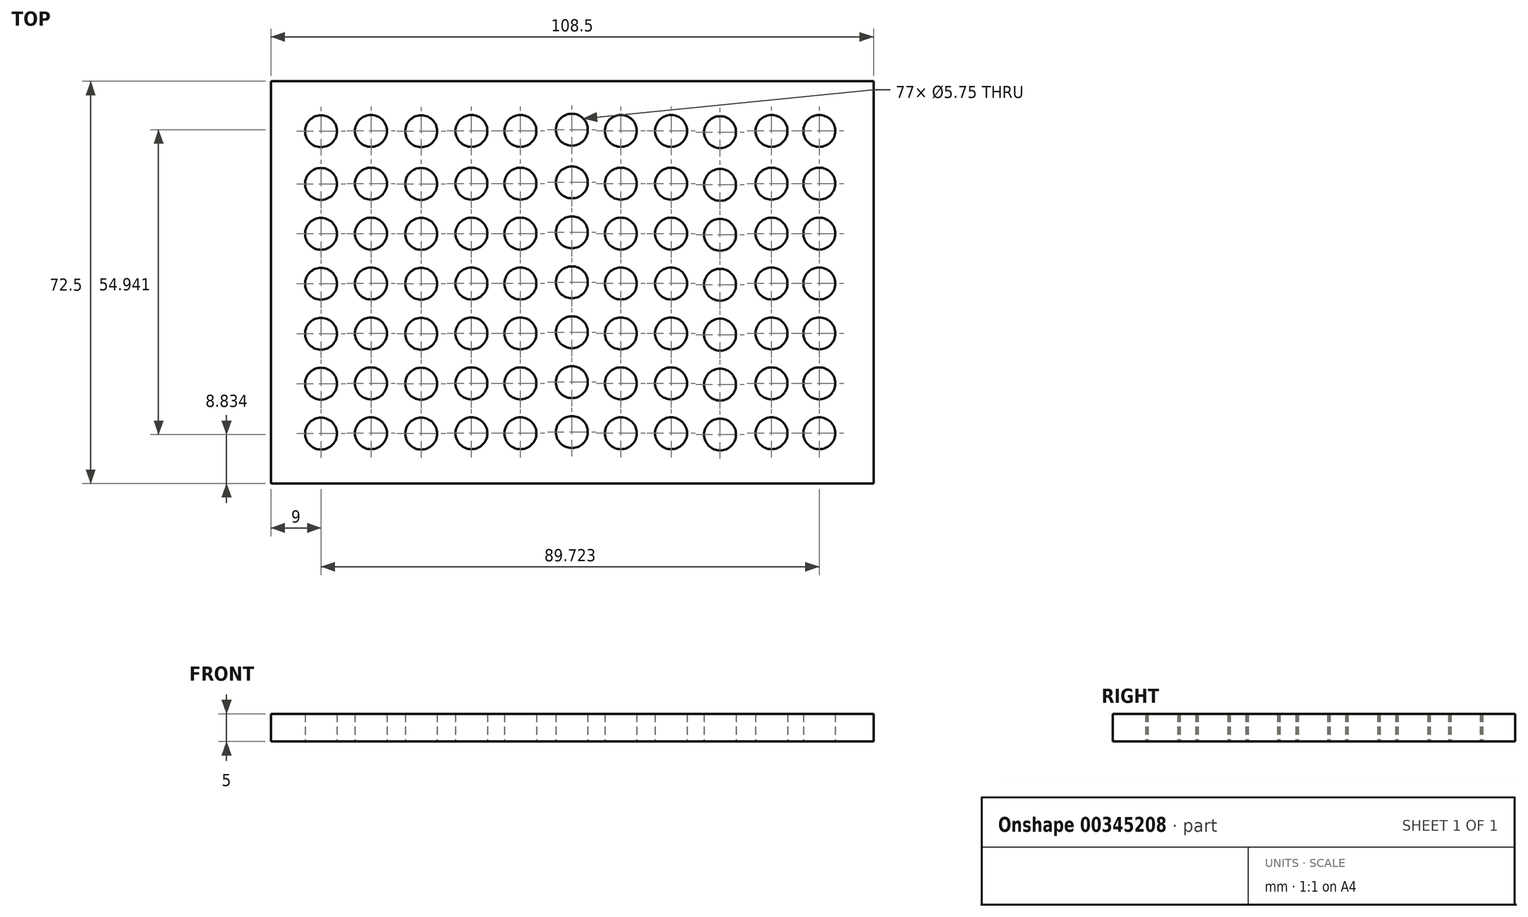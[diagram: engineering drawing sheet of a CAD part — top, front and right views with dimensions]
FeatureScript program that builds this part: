
annotation { "Feature Type Name" : "Feature", "Feature Type Description" : "" }
export const myFeature = defineFeature(function(context is Context, id is Id, definition is map)
    precondition{}
    {
        {
            var Q0;
            Q0=qCreatedBy(makeId("Top.planeOp"),FACE);
            var sketch = newSketch(context, id + "F0", { "sketchPlane" : qUnion([Q0])});
            skLineSegment(sketch, "E0", {"start": v(0, 0) * mm, "end": v(0, 72.5) * mm});
            skLineSegment(sketch, "E1", {"start": v(0, 0) * mm, "end": v(108.5, 0) * mm});
            skLineSegment(sketch, "E2", {"start": v(0, 72.5) * mm, "end": v(108.5, 72.5) * mm});
            skLineSegment(sketch, "E3", {"start": v(108.5, 72.5) * mm, "end": v(108.5, 0) * mm});
            skLineSegment(sketch, "E4", {"start": v(0, 0) * mm, "end": v(9, 0) * mm});
            skLineSegment(sketch, "E5", {"start": v(0, 72.5) * mm, "end": v(0, 63.5) * mm});
            skLineSegment(sketch, "E6", {"start": v(0, 0) * mm, "end": v(0, 9) * mm});
            skLineSegment(sketch, "E7", {"start": v(108.5, 9) * mm, "end": v(108.5, 18) * mm});
            skLineSegment(sketch, "E8", {"start": v(0, 18) * mm, "end": v(0, 27) * mm});
            skLineSegment(sketch, "E9", {"start": v(108.5, 27) * mm, "end": v(108.5, 36) * mm});
            skLineSegment(sketch, "E10", {"start": v(0, 36) * mm, "end": v(0, 45) * mm});
            skLineSegment(sketch, "E11", {"start": v(108.5, 45) * mm, "end": v(108.5, 54) * mm});
            skLineSegment(sketch, "E12", {"start": v(9, 72.5) * mm, "end": v(18, 72.5) * mm});
            skLineSegment(sketch, "E13", {"start": v(18, 72.5) * mm, "end": v(27, 72.5) * mm});
            skLineSegment(sketch, "E14", {"start": v(27, 72.5) * mm, "end": v(36, 72.5) * mm});
            skLineSegment(sketch, "E15", {"start": v(36, 72.5) * mm, "end": v(54.25, 72.5) * mm});
            skLineSegment(sketch, "E16", {"start": v(36, 72.5) * mm, "end": v(45, 72.5) * mm});
            skLineSegment(sketch, "E17", {"start": v(45, 72.5) * mm, "end": v(54, 72.5) * mm});
            skLineSegment(sketch, "E18", {"start": v(54, 72.5) * mm, "end": v(63, 72.5) * mm});
            skLineSegment(sketch, "E19", {"start": v(63, 72.5) * mm, "end": v(72, 72.5) * mm});
            skLineSegment(sketch, "E20", {"start": v(72, 72.5) * mm, "end": v(81, 72.5) * mm});
            skLineSegment(sketch, "E21", {"start": v(81, 72.5) * mm, "end": v(90, 72.5) * mm});
            skLineSegment(sketch, "E22", {"start": v(90, 72.5) * mm, "end": v(99, 72.5) * mm});
            skLineSegment(sketch, "E23", {"start": v(99, 72.5) * mm, "end": v(108.5, 72.5) * mm});
            skCircle(sketch, "E24", {"center": v(9, 63.5) * mm, "radius": 2.88 * mm});
            skCircle(sketch, "E25", {"center": v(9, 54) * mm, "radius": 2.88 * mm});
            skCircle(sketch, "E26", {"center": v(9, 45) * mm, "radius": 2.88 * mm});
            skCircle(sketch, "E27", {"center": v(9, 36) * mm, "radius": 2.88 * mm});
            skPoint(sketch, "E27.centerSnap0", {"position": v(9, 36.25) * mm});
            skCircle(sketch, "E28", {"center": v(9, 27) * mm, "radius": 2.88 * mm});
            skCircle(sketch, "E29", {"center": v(9, 18) * mm, "radius": 2.88 * mm});
            skCircle(sketch, "E30", {"center": v(9, 9) * mm, "radius": 2.88 * mm});
            skCircle(sketch, "E31", {"center": v(18, 63.55) * mm, "radius": 2.88 * mm});
            skCircle(sketch, "E32", {"center": v(18, 54.05) * mm, "radius": 2.88 * mm});
            skCircle(sketch, "E33", {"center": v(18, 45.05) * mm, "radius": 2.88 * mm});
            skCircle(sketch, "E34", {"center": v(18, 36.05) * mm, "radius": 2.88 * mm});
            skPoint(sketch, "E34.centerSnap0", {"position": v(18, 36.3) * mm});
            skCircle(sketch, "E35", {"center": v(18, 27.05) * mm, "radius": 2.88 * mm});
            skCircle(sketch, "E36", {"center": v(18, 18.05) * mm, "radius": 2.88 * mm});
            skCircle(sketch, "E37", {"center": v(18, 9.05) * mm, "radius": 2.88 * mm});
            skCircle(sketch, "E38", {"center": v(27.04, 63.5) * mm, "radius": 2.88 * mm});
            skCircle(sketch, "E39", {"center": v(27.04, 54) * mm, "radius": 2.88 * mm});
            skCircle(sketch, "E40", {"center": v(27.04, 45) * mm, "radius": 2.88 * mm});
            skCircle(sketch, "E41", {"center": v(27.04, 36) * mm, "radius": 2.88 * mm});
            skPoint(sketch, "E41.centerSnap0", {"position": v(27.04, 36.25) * mm});
            skCircle(sketch, "E42", {"center": v(27.04, 27) * mm, "radius": 2.88 * mm});
            skCircle(sketch, "E43", {"center": v(27.04, 18) * mm, "radius": 2.88 * mm});
            skCircle(sketch, "E44", {"center": v(27.04, 9) * mm, "radius": 2.88 * mm});
            skCircle(sketch, "E45", {"center": v(36.08, 63.55) * mm, "radius": 2.88 * mm});
            skCircle(sketch, "E46", {"center": v(36.08, 54.05) * mm, "radius": 2.88 * mm});
            skCircle(sketch, "E47", {"center": v(36.08, 45.05) * mm, "radius": 2.88 * mm});
            skCircle(sketch, "E48", {"center": v(36.08, 36.05) * mm, "radius": 2.88 * mm});
            skPoint(sketch, "E48.centerSnap0", {"position": v(36.08, 36.3) * mm});
            skCircle(sketch, "E49", {"center": v(36.08, 27.05) * mm, "radius": 2.88 * mm});
            skCircle(sketch, "E50", {"center": v(36.08, 18.05) * mm, "radius": 2.88 * mm});
            skCircle(sketch, "E51", {"center": v(36.08, 9.05) * mm, "radius": 2.88 * mm});
            skCircle(sketch, "E52", {"center": v(44.9, 63.55) * mm, "radius": 2.88 * mm});
            skCircle(sketch, "E53", {"center": v(44.9, 54.05) * mm, "radius": 2.88 * mm});
            skCircle(sketch, "E54", {"center": v(44.9, 45.05) * mm, "radius": 2.88 * mm});
            skCircle(sketch, "E55", {"center": v(44.9, 36.05) * mm, "radius": 2.88 * mm});
            skPoint(sketch, "E55.centerSnap0", {"position": v(44.9, 36.3) * mm});
            skCircle(sketch, "E56", {"center": v(44.9, 27.05) * mm, "radius": 2.88 * mm});
            skCircle(sketch, "E57", {"center": v(44.9, 18.05) * mm, "radius": 2.88 * mm});
            skCircle(sketch, "E58", {"center": v(44.9, 9.05) * mm, "radius": 2.88 * mm});
            skCircle(sketch, "E59", {"center": v(54.17, 63.77) * mm, "radius": 2.88 * mm});
            skCircle(sketch, "E60", {"center": v(54.17, 54.27) * mm, "radius": 2.88 * mm});
            skCircle(sketch, "E61", {"center": v(54.17, 45.27) * mm, "radius": 2.88 * mm});
            skCircle(sketch, "E62", {"center": v(54.17, 36.27) * mm, "radius": 2.88 * mm});
            skPoint(sketch, "E62.centerSnap0", {"position": v(54.17, 36.52) * mm});
            skCircle(sketch, "E63", {"center": v(54.17, 27.27) * mm, "radius": 2.88 * mm});
            skCircle(sketch, "E64", {"center": v(54.17, 18.27) * mm, "radius": 2.88 * mm});
            skCircle(sketch, "E65", {"center": v(54.17, 9.27) * mm, "radius": 2.88 * mm});
            skCircle(sketch, "E66", {"center": v(63, 63.55) * mm, "radius": 2.88 * mm});
            skCircle(sketch, "E67", {"center": v(63, 54.05) * mm, "radius": 2.88 * mm});
            skCircle(sketch, "E68", {"center": v(63, 45.05) * mm, "radius": 2.88 * mm});
            skCircle(sketch, "E69", {"center": v(63, 36.05) * mm, "radius": 2.88 * mm});
            skPoint(sketch, "E69.centerSnap0", {"position": v(63, 36.3) * mm});
            skCircle(sketch, "E70", {"center": v(63, 27.05) * mm, "radius": 2.88 * mm});
            skCircle(sketch, "E71", {"center": v(63, 18.05) * mm, "radius": 2.88 * mm});
            skCircle(sketch, "E72", {"center": v(63, 9.05) * mm, "radius": 2.88 * mm});
            skCircle(sketch, "E73", {"center": v(72.03, 63.55) * mm, "radius": 2.88 * mm});
            skCircle(sketch, "E74", {"center": v(72.03, 54.05) * mm, "radius": 2.88 * mm});
            skCircle(sketch, "E75", {"center": v(72.03, 45.05) * mm, "radius": 2.88 * mm});
            skCircle(sketch, "E76", {"center": v(72.03, 36.05) * mm, "radius": 2.88 * mm});
            skPoint(sketch, "E76.centerSnap0", {"position": v(72.03, 36.3) * mm});
            skCircle(sketch, "E77", {"center": v(72.03, 27.05) * mm, "radius": 2.88 * mm});
            skCircle(sketch, "E78", {"center": v(72.03, 18.05) * mm, "radius": 2.88 * mm});
            skCircle(sketch, "E79", {"center": v(72.03, 9.05) * mm, "radius": 2.88 * mm});
            skCircle(sketch, "E80", {"center": v(80.86, 63.33) * mm, "radius": 2.88 * mm});
            skCircle(sketch, "E81", {"center": v(80.86, 53.83) * mm, "radius": 2.88 * mm});
            skCircle(sketch, "E82", {"center": v(80.86, 44.83) * mm, "radius": 2.88 * mm});
            skCircle(sketch, "E83", {"center": v(80.86, 35.83) * mm, "radius": 2.88 * mm});
            skPoint(sketch, "E83.centerSnap0", {"position": v(80.86, 36.08) * mm});
            skCircle(sketch, "E84", {"center": v(80.86, 26.83) * mm, "radius": 2.88 * mm});
            skCircle(sketch, "E85", {"center": v(80.86, 17.83) * mm, "radius": 2.88 * mm});
            skCircle(sketch, "E86", {"center": v(80.86, 8.83) * mm, "radius": 2.88 * mm});
            skCircle(sketch, "E87", {"center": v(90.12, 63.55) * mm, "radius": 2.88 * mm});
            skCircle(sketch, "E88", {"center": v(90.12, 54.05) * mm, "radius": 2.88 * mm});
            skCircle(sketch, "E89", {"center": v(90.12, 45.05) * mm, "radius": 2.88 * mm});
            skCircle(sketch, "E90", {"center": v(90.12, 36.05) * mm, "radius": 2.88 * mm});
            skPoint(sketch, "E90.centerSnap0", {"position": v(90.12, 36.3) * mm});
            skCircle(sketch, "E91", {"center": v(90.12, 27.05) * mm, "radius": 2.88 * mm});
            skCircle(sketch, "E92", {"center": v(90.12, 18.05) * mm, "radius": 2.88 * mm});
            skCircle(sketch, "E93", {"center": v(90.12, 9.05) * mm, "radius": 2.88 * mm});
            skCircle(sketch, "E94", {"center": v(98.72, 63.55) * mm, "radius": 2.88 * mm});
            skCircle(sketch, "E95", {"center": v(98.72, 54.05) * mm, "radius": 2.88 * mm});
            skCircle(sketch, "E96", {"center": v(98.72, 45.05) * mm, "radius": 2.88 * mm});
            skCircle(sketch, "E97", {"center": v(98.72, 36.05) * mm, "radius": 2.88 * mm});
            skPoint(sketch, "E97.centerSnap0", {"position": v(98.72, 36.3) * mm});
            skCircle(sketch, "E98", {"center": v(98.72, 27.05) * mm, "radius": 2.88 * mm});
            skCircle(sketch, "E99", {"center": v(98.72, 18.05) * mm, "radius": 2.88 * mm});
            skCircle(sketch, "E100", {"center": v(98.72, 9.05) * mm, "radius": 2.88 * mm});
            skSolve(sketch);
        }
        {
            var Q0;
            {var subQ8=sQuery(id+"F0.wireOp",EDGE,"E1");Q0=makeQuery(id+"F0.imprint","IMPRINT",FACE,{"disambiguationData":[TD([[makeQuery(id+"F0.imprint","IMPRINT",EDGE,{"derivedFrom":subQ8}),1.0]])]});}
            extrude(context, id + "F1", {"entities" : qUnion([Q0]), "depth" : 5 * mm});
        }
    });
